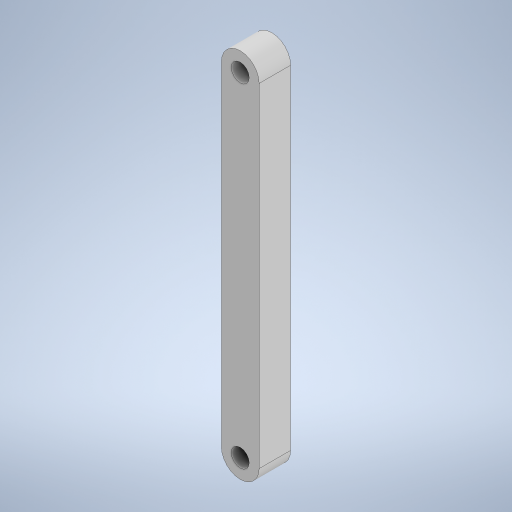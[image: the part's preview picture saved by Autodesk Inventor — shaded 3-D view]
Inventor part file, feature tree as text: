
AUTODESK INVENTOR PART (.ipt)
format: ipt  version: 2023 (Build 270158000, 158)  size: 241,664 bytes
history: native  units: mm
features: extrude x1, sketch x1
ambient origin geometry x8: Origin, YZ Plane, XZ Plane, XY Plane, X Axis, Y Axis, Z Axis, Center Point
bodies: Solid1 (feature_tree)
feature tree (2):
  extrude  "Extrusion1"  Depth=6.0mm
  sketch  "Sketch1"  dims[d8=5.0mm d9=0.0mm d10=6.0mm d11=59.0mm d12=3.0mm d13=6.0mm d14=2.85mm d15=3.0mm d16=6.0mm d17=2.85mm]
